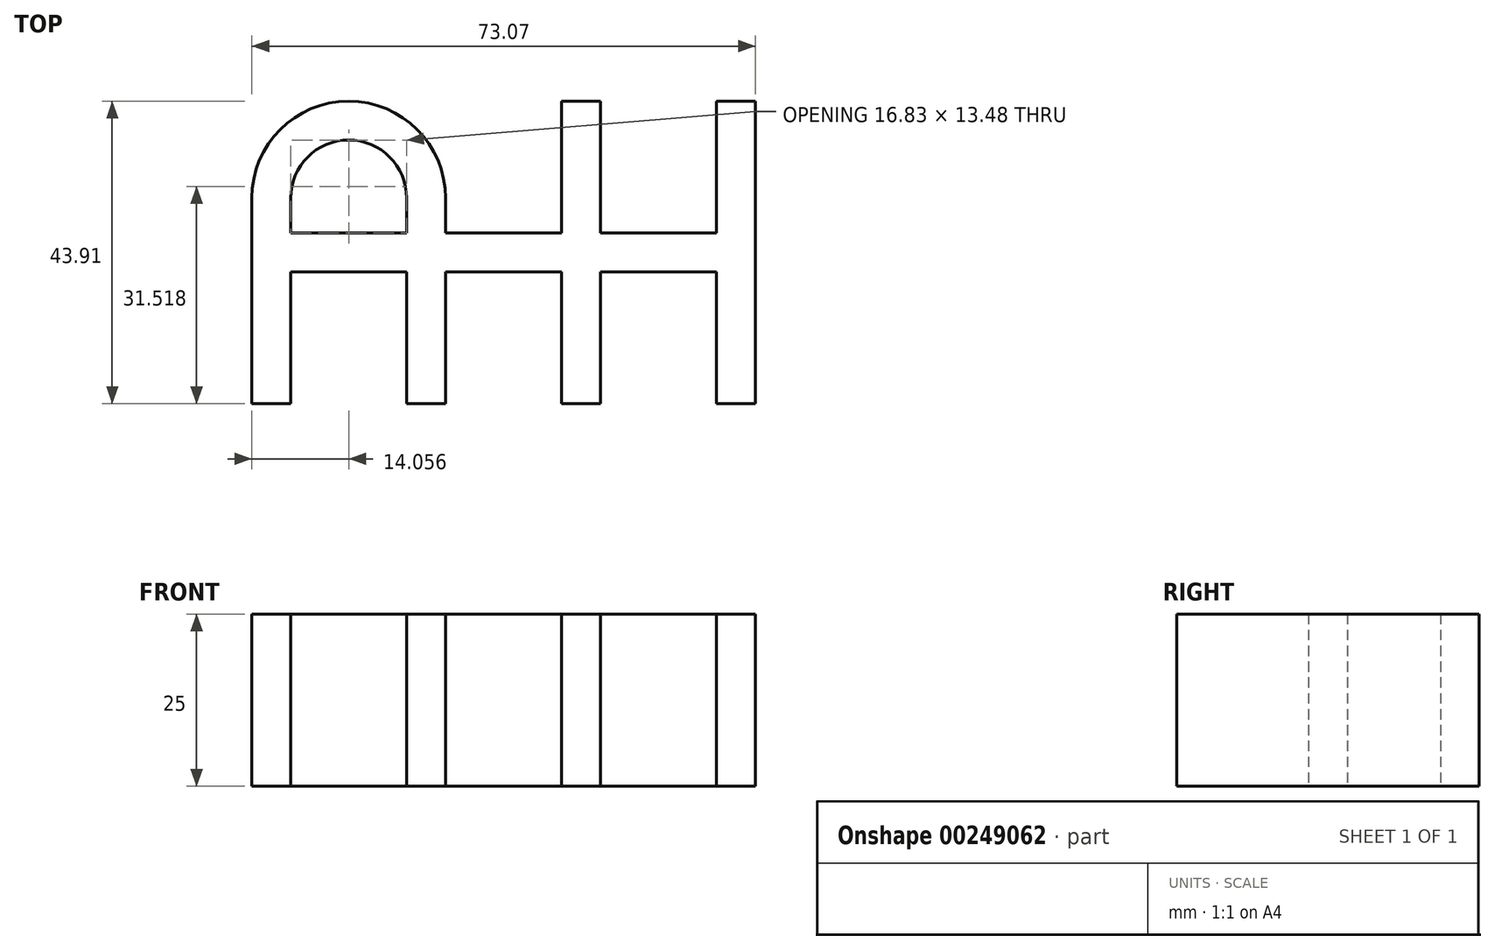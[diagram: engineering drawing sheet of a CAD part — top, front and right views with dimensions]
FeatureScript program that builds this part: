
annotation { "Feature Type Name" : "Feature", "Feature Type Description" : "" }
export const myFeature = defineFeature(function(context is Context, id is Id, definition is map)
    precondition{}
    {
        {
            var Q0;
            Q0=qCreatedBy(makeId("Top.planeOp"),FACE);
            var sketch = newSketch(context, id + "F0", { "sketchPlane" : qUnion([Q0])});
            skLineSegment(sketch, "E0", {"start": v(0, 0) * mm, "end": v(5.65, 0) * mm});
            skLineSegment(sketch, "E1", {"start": v(5.65, 0) * mm, "end": v(5.65, 19.13) * mm});
            skLineSegment(sketch, "E2", {"start": v(5.65, 19.13) * mm, "end": v(22.47, 19.13) * mm});
            skLineSegment(sketch, "E3", {"start": v(22.47, 19.13) * mm, "end": v(22.47, 0) * mm});
            skLineSegment(sketch, "E4", {"start": v(22.47, 0) * mm, "end": v(28.12, 0) * mm});
            skLineSegment(sketch, "E5", {"start": v(28.12, 0) * mm, "end": v(28.12, 19.13) * mm});
            skLineSegment(sketch, "E6", {"start": v(28.12, 19.13) * mm, "end": v(44.95, 19.13) * mm});
            skLineSegment(sketch, "E7", {"start": v(44.95, 19.13) * mm, "end": v(44.95, 0) * mm});
            skLineSegment(sketch, "E8", {"start": v(44.95, 0) * mm, "end": v(50.6, 0) * mm});
            skLineSegment(sketch, "E9", {"start": v(50.6, 0) * mm, "end": v(50.6, 43.9) * mm});
            skLineSegment(sketch, "E10", {"start": v(50.6, 43.9) * mm, "end": v(44.95, 43.9) * mm});
            skLineSegment(sketch, "E11", {"start": v(44.95, 43.9) * mm, "end": v(44.95, 24.78) * mm});
            skLineSegment(sketch, "E12", {"start": v(44.95, 24.78) * mm, "end": v(28.12, 24.78) * mm});
            skLineSegment(sketch, "E13", {"start": v(28.12, 24.78) * mm, "end": v(28.12, 43.9) * mm});
            skLineSegment(sketch, "E14", {"start": v(28.12, 43.9) * mm, "end": v(22.47, 43.9) * mm});
            skLineSegment(sketch, "E15", {"start": v(22.47, 43.9) * mm, "end": v(22.47, 24.78) * mm});
            skLineSegment(sketch, "E16", {"start": v(22.47, 24.78) * mm, "end": v(5.65, 24.78) * mm});
            skLineSegment(sketch, "E17", {"start": v(5.65, 24.78) * mm, "end": v(5.65, 29.84) * mm});
            skLineSegment(sketch, "E18", {"start": v(0, 0) * mm, "end": v(0, 19.13) * mm});
            skLineSegment(sketch, "E19", {"start": v(0, 19.13) * mm, "end": v(-16.83, 19.13) * mm});
            skLineSegment(sketch, "E20", {"start": v(-16.83, 19.13) * mm, "end": v(-16.83, 0) * mm});
            skLineSegment(sketch, "E21", {"start": v(-16.83, 0) * mm, "end": v(-22.47, 0) * mm});
            skLineSegment(sketch, "E22", {"start": v(-22.47, 0) * mm, "end": v(-22.47, 29.84) * mm});
            skArc(sketch, "E23", {"start": v(5.65, 29.84) * mm, "mid": v(-8.41, 43.9) * mm, "end": v(-22.47, 29.84) * mm});
            skLineSegment(sketch, "E24", {"start": v(0, 24.78) * mm, "end": v(-16.83, 24.78) * mm});
            skLineSegment(sketch, "E25", {"start": v(-16.83, 24.78) * mm, "end": v(-16.83, 29.84) * mm});
            skLineSegment(sketch, "E26", {"start": v(0, 24.78) * mm, "end": v(0, 29.84) * mm});
            skArc(sketch, "E27", {"start": v(0, 29.84) * mm, "mid": v(-8.41, 38.26) * mm, "end": v(-16.83, 29.84) * mm});
            skLineSegment(sketch, "E28", {"start": v(-8.41, 43.9) * mm, "end": v(22.47, 43.9) * mm, "construction": true});
            skLineSegment(sketch, "E29", {"start": v(44.95, 24.78) * mm, "end": v(44.95, 19.13) * mm, "construction": true});
            skSolve(sketch);
        }
        {
            var Q0;
            Q0 = qSketchRegion(id + "F0", true);
            extrude(context, id + "F1", {"entities" : qUnion([Q0]), "depth" : 25 * mm});
        }
    });
